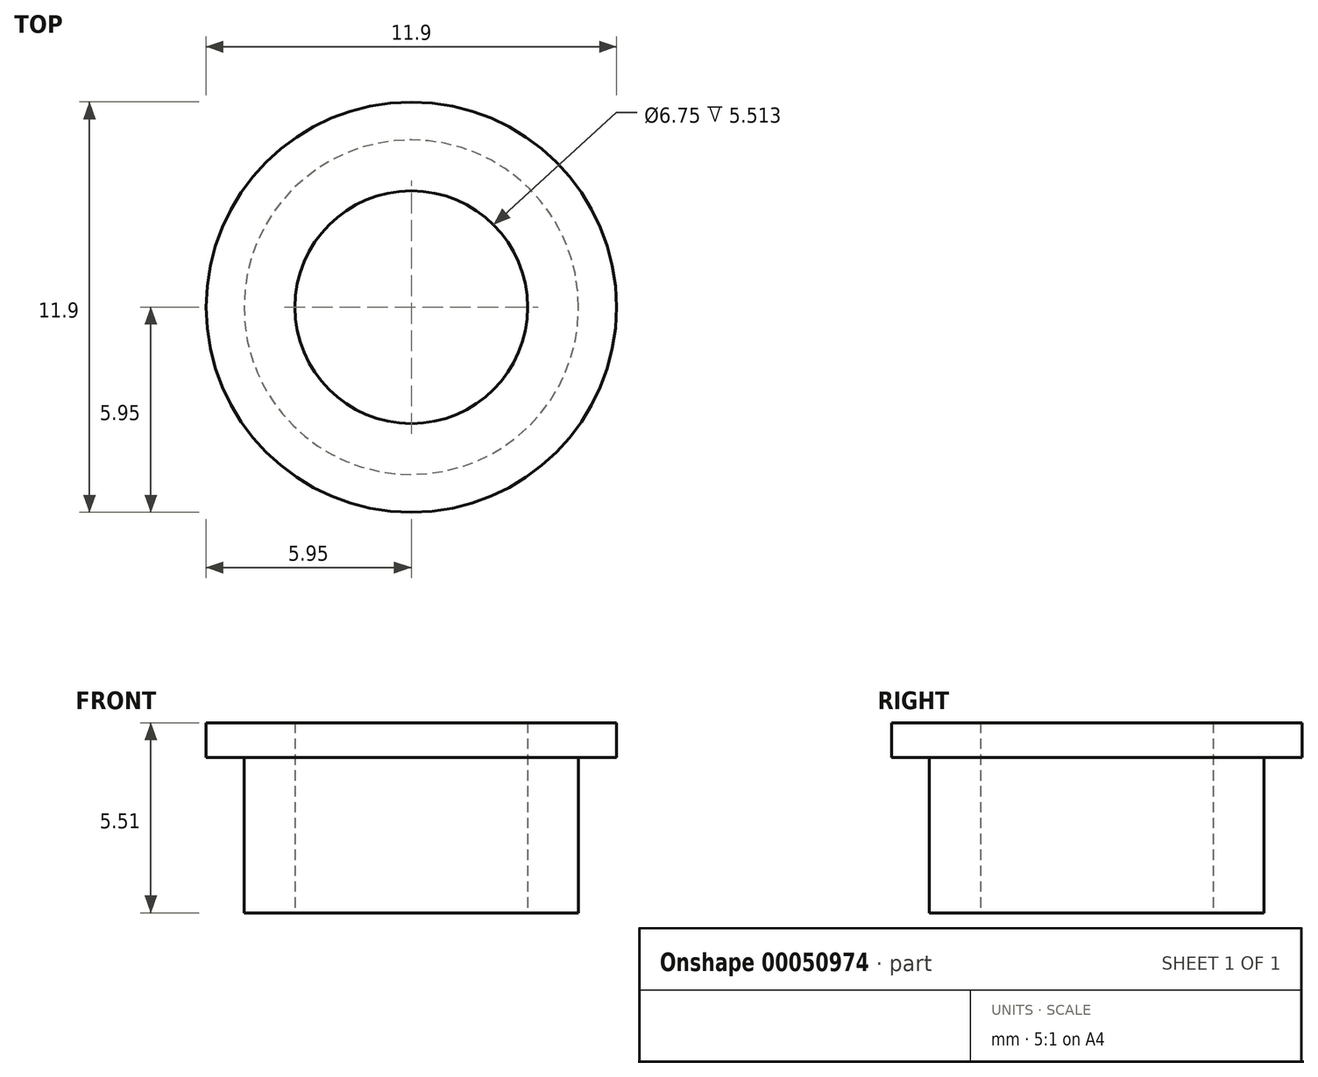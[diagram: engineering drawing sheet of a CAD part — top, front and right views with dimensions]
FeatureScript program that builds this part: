
annotation { "Feature Type Name" : "Feature", "Feature Type Description" : "" }
export const myFeature = defineFeature(function(context is Context, id is Id, definition is map)
    precondition{}
    {
        {
            var Q0;
            Q0=qCreatedBy(makeId("Right.planeOp"),FACE);
            var sketch = newSketch(context, id + "F0", { "sketchPlane" : qUnion([Q0])});
            skLineSegment(sketch, "E0", {"start": v(-4.85, 4.5) * mm, "end": v(-5.95, 4.5) * mm});
            skLineSegment(sketch, "E1", {"start": v(-5.95, 4.5) * mm, "end": v(-5.95, 5.51) * mm});
            skLineSegment(sketch, "E2", {"start": v(-5.95, 5.51) * mm, "end": v(0, 5.51) * mm});
            skLineSegment(sketch, "E3", {"start": v(0, 0) * mm, "end": v(-4.85, 0) * mm});
            skLineSegment(sketch, "E4", {"start": v(-4.85, 0) * mm, "end": v(-4.85, 4.5) * mm});
            skLineSegment(sketch, "E5", {"start": v(0, 5.51) * mm, "end": v(0, 0) * mm});
            skSolve(sketch);
        }
        {
            var Q0;
            Q0=makeQuery(id+"F0.imprint","IMPRINT",FACE,{"disambiguationData":[TD([[makeQuery(id+"F0.imprint","IMPRINT",EDGE,{"derivedFrom":sQuery(id+"F0.wireOp",EDGE,"E0")}),-1.0]])]});
            var Q1;
            Q1=sQuery(id+"F0.wireOp",EDGE,"E5");
            revolve(context, id + "F1", {"entities" : qUnion([Q0]), "axis" : qUnion([Q1]), "revolveType" : RevolveType.FULL});
        }
        {
            var Q0;
            Q0=qCreatedBy(makeId("Top.planeOp"),FACE);
            var sketch = newSketch(context, id + "F2", { "sketchPlane" : qUnion([Q0])});
            skCircle(sketch, "E6", {"center": v(0, 0) * mm, "radius": 3.38 * mm});
            skSolve(sketch);
        }
        {
            var Q0;
            Q0 = qSketchRegion(id + "F2", true);
            extrude(context, id + "F3", {"entities" : qUnion([Q0]), "operationType" : NewBodyOperationType.REMOVE, "depth" : 6.77 * mm});
        }
    });
